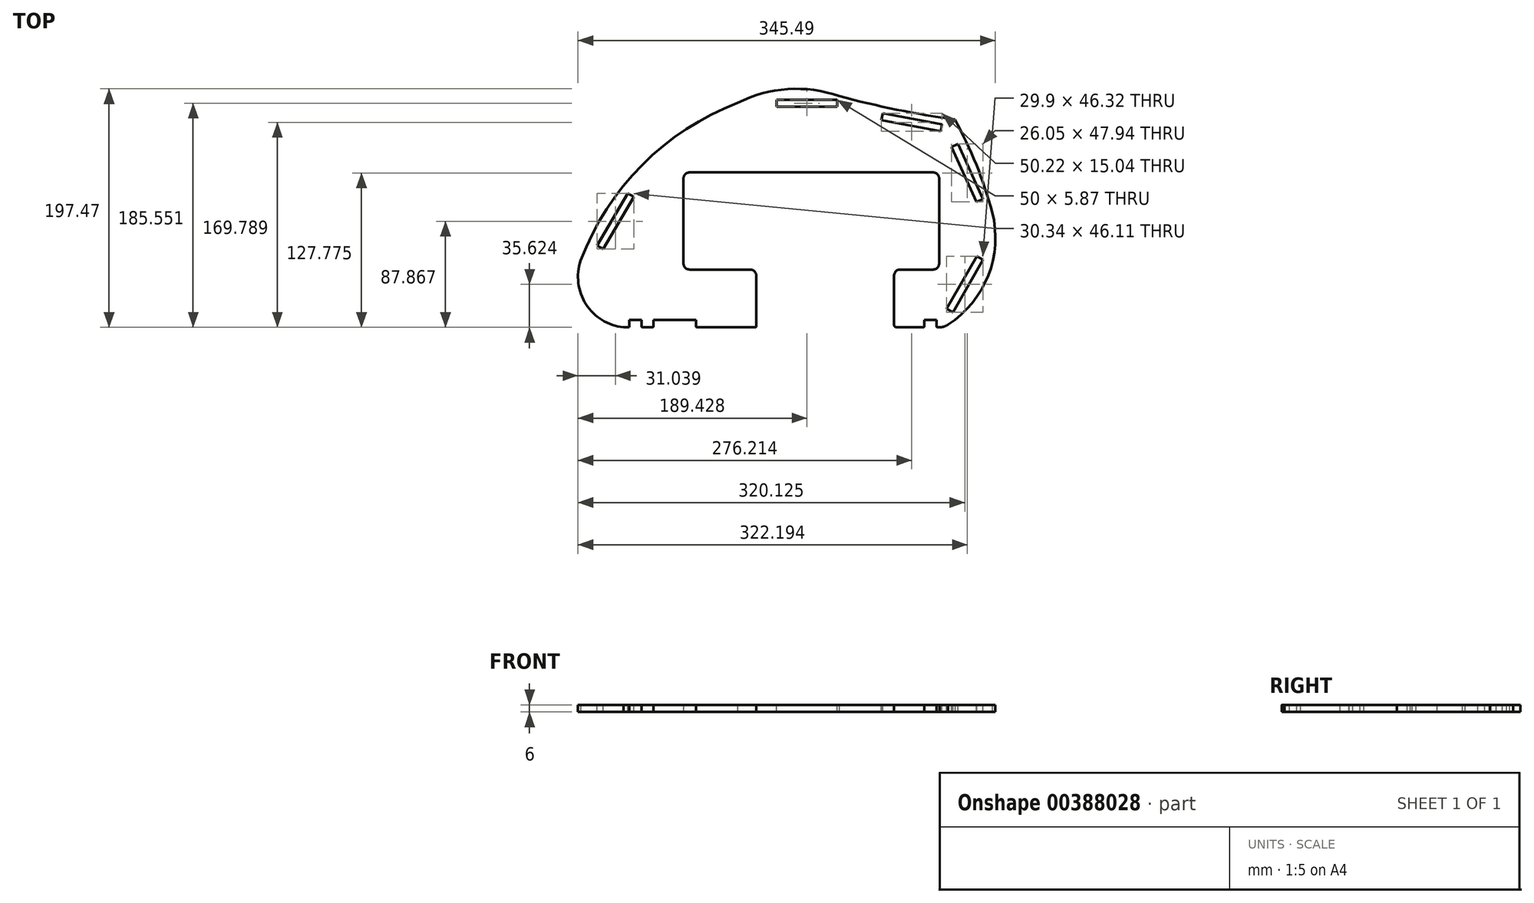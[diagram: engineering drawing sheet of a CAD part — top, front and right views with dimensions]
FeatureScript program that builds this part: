
annotation { "Feature Type Name" : "Feature", "Feature Type Description" : "" }
export const myFeature = defineFeature(function(context is Context, id is Id, definition is map)
    precondition{}
    {
        {
            var Q0;
            Q0=qCreatedBy(makeId("Top.planeOp"),FACE);
            var sketch = newSketch(context, id + "F0", { "sketchPlane" : qUnion([Q0])});
            skArc(sketch, "E0.0", {"start": v(177.07, -17.22) * mm, "mid": v(210.31, 23.38) * mm, "end": v(213.66, 75.75) * mm});
            skArc(sketch, "E1.0", {"start": v(170.2, -19.39) * mm, "mid": v(173.8, -18.84) * mm, "end": v(177.07, -17.22) * mm});
            skArc(sketch, "E2.0", {"start": v(-126.92, 35.78) * mm, "mid": v(-122.64, -0.38) * mm, "end": v(-91.61, -19.43) * mm});
            skArc(sketch, "E3.0", {"start": v(86.99, 172) * mm, "mid": v(44.36, 177.73) * mm, "end": v(2.91, 166.26) * mm});
            skArc(sketch, "E4", {"start": v(2.91, 166.26) * mm, "mid": v(-76.08, 115.03) * mm, "end": v(-126.92, 35.78) * mm});
            skArc(sketch, "E5", {"start": v(213.66, 75.75) * mm, "mid": v(200.48, 115.15) * mm, "end": v(182.68, 152.69) * mm});
            skLineSegment(sketch, "E6.0", {"start": v(157.44, -13.49) * mm, "end": v(157.44, -18.49) * mm});
            skLineSegment(sketch, "E7.0", {"start": v(132.44, -13.49) * mm, "end": v(132.44, -17.49) * mm});
            skLineSegment(sketch, "E8.0", {"start": v(-31.66, -13.49) * mm, "end": v(-31.66, -18.49) * mm});
            skLineSegment(sketch, "E8.1", {"start": v(-76.66, -13.49) * mm, "end": v(-76.66, -18.49) * mm});
            skLineSegment(sketch, "E9.0", {"start": v(-66.66, -13.49) * mm, "end": v(-66.66, -18.49) * mm});
            skLineSegment(sketch, "E9.1", {"start": v(18.34, -13.49) * mm, "end": v(18.34, -18.49) * mm});
            skLineSegment(sketch, "E10.0", {"start": v(167.44, -18.45) * mm, "end": v(167.44, -13.49) * mm});
            skLineSegment(sketch, "E11.0", {"start": v(-86.66, -13.49) * mm, "end": v(-86.66, -19.49) * mm});
            skLineSegment(sketch, "E12", {"start": v(167.44, -13.49) * mm, "end": v(157.44, -13.49) * mm});
            skLineSegment(sketch, "E13", {"start": v(-31.66, -13.49) * mm, "end": v(-66.66, -13.49) * mm});
            skLineSegment(sketch, "E14", {"start": v(-76.66, -13.49) * mm, "end": v(-86.66, -13.49) * mm});
            skLineSegment(sketch, "E15", {"start": v(170.2, -19.39) * mm, "end": v(168.47, -19.45) * mm});
            skLineSegment(sketch, "E16", {"start": v(156.44, -19.49) * mm, "end": v(134.44, -19.49) * mm});
            skLineSegment(sketch, "E17", {"start": v(-75.66, -19.49) * mm, "end": v(-67.66, -19.49) * mm});
            skLineSegment(sketch, "E18", {"start": v(-30.66, -19.49) * mm, "end": v(17.34, -19.49) * mm});
            skLineSegment(sketch, "E19", {"start": v(-91.61, -19.43) * mm, "end": v(-86.66, -19.49) * mm});
            skPoint(sketch, "E20.visualSharp", {"position": v(157.44, -19.49) * mm});
            skArc(sketch, "E20.filletArc", {"start": v(156.44, -19.49) * mm, "mid": v(157.15, -19.2) * mm, "end": v(157.44, -18.49) * mm});
            skPoint(sketch, "E21.visualSharp", {"position": v(132.44, -19.49) * mm});
            skArc(sketch, "E21.filletArc", {"start": v(132.44, -17.49) * mm, "mid": v(133.03, -18.9) * mm, "end": v(134.44, -19.49) * mm});
            skPoint(sketch, "E22.visualSharp", {"position": v(167.44, -19.49) * mm});
            skArc(sketch, "E22.filletArc", {"start": v(167.44, -18.45) * mm, "mid": v(167.75, -19.17) * mm, "end": v(168.47, -19.45) * mm});
            skPoint(sketch, "E23.visualSharp", {"position": v(-76.66, -19.49) * mm});
            skArc(sketch, "E23.filletArc", {"start": v(-76.66, -18.49) * mm, "mid": v(-76.37, -19.2) * mm, "end": v(-75.66, -19.49) * mm});
            skPoint(sketch, "E24.visualSharp", {"position": v(-66.66, -19.49) * mm});
            skArc(sketch, "E24.filletArc", {"start": v(-67.66, -19.49) * mm, "mid": v(-66.95, -19.2) * mm, "end": v(-66.66, -18.49) * mm});
            skPoint(sketch, "E25.visualSharp", {"position": v(-31.66, -19.49) * mm});
            skArc(sketch, "E25.filletArc", {"start": v(-31.66, -18.49) * mm, "mid": v(-31.37, -19.2) * mm, "end": v(-30.66, -19.49) * mm});
            skPoint(sketch, "E26.visualSharp", {"position": v(18.34, -19.49) * mm});
            skArc(sketch, "E26.filletArc", {"start": v(17.34, -19.49) * mm, "mid": v(18.05, -19.2) * mm, "end": v(18.34, -18.49) * mm});
            skLineSegment(sketch, "E27", {"start": v(132.44, -13.49) * mm, "end": v(132.44, 28.36) * mm});
            skLineSegment(sketch, "E28", {"start": v(132.44, 28.36) * mm, "end": v(169.69, 28.36) * mm});
            skLineSegment(sketch, "E29", {"start": v(169.69, 28.36) * mm, "end": v(169.69, 108.76) * mm});
            skLineSegment(sketch, "E30", {"start": v(-41.86, 28.36) * mm, "end": v(18.34, 28.36) * mm});
            skLineSegment(sketch, "E31", {"start": v(18.34, 28.36) * mm, "end": v(18.34, -13.49) * mm});
            skLineSegment(sketch, "E32", {"start": v(-41.86, 28.36) * mm, "end": v(-41.86, 108.76) * mm});
            skLineSegment(sketch, "E33", {"start": v(-41.86, 108.76) * mm, "end": v(169.69, 108.76) * mm});
            skArc(sketch, "E34", {"start": v(86.99, 172) * mm, "mid": v(134.51, 160.75) * mm, "end": v(182.68, 152.69) * mm});
            skSolve(sketch);
        }
        {
            var Q0;
            Q0 = qSketchRegion(id + "F0", true);
            extrude(context, id + "F1", {"entities" : qUnion([Q0]), "depth" : 6 * mm});
        }
        {
            var Q0;
            Q0=makeQuery(id+"F1.opExtrude","SWEPT_EDGE",EDGE,{"disambiguationData":[OSD([sQuery(id+"F0.wireOp",EDGE,"E32"),sQuery(id+"F0.wireOp",EDGE,"E33")])]});
            var Q1;
            Q1=makeQuery(id+"F1.opExtrude","SWEPT_EDGE",EDGE,{"disambiguationData":[OSD([sQuery(id+"F0.wireOp",EDGE,"E30"),sQuery(id+"F0.wireOp",EDGE,"E32")])]});
            var Q2;
            Q2=makeQuery(id+"F1.opExtrude","SWEPT_EDGE",EDGE,{"disambiguationData":[OSD([sQuery(id+"F0.wireOp",EDGE,"E30"),sQuery(id+"F0.wireOp",EDGE,"E31")])]});
            var Q3;
            Q3=makeQuery(id+"F1.opExtrude","SWEPT_EDGE",EDGE,{"disambiguationData":[OSD([sQuery(id+"F0.wireOp",EDGE,"E29"),sQuery(id+"F0.wireOp",EDGE,"E33")])]});
            var Q4;
            Q4=makeQuery(id+"F1.opExtrude","SWEPT_EDGE",EDGE,{"disambiguationData":[OSD([sQuery(id+"F0.wireOp",EDGE,"E28"),sQuery(id+"F0.wireOp",EDGE,"E29")])]});
            var Q5;
            Q5=makeQuery(id+"F1.opExtrude","SWEPT_EDGE",EDGE,{"disambiguationData":[OSD([sQuery(id+"F0.wireOp",EDGE,"E27"),sQuery(id+"F0.wireOp",EDGE,"E28")])]});
            fillet(context, id + "F2", {"entities" : qUnion([Q0, Q1, Q2, Q3, Q4, Q5]), "radius" : 5 * mm, "tangentPropagation" : true, "allowEdgeOverflow" : false});
        }
        {
            var Q0;
            Q0=makeQuery(id+"F1.opExtrude","CAP_FACE",FACE,{"disambiguationData":[OSD([sQuery(id+"F0.wireOp",EDGE,"E0.0"),sQuery(id+"F0.wireOp",EDGE,"E1.0"),sQuery(id+"F0.wireOp",EDGE,"E2.0"),sQuery(id+"F0.wireOp",EDGE,"E3.0"),sQuery(id+"F0.wireOp",EDGE,"623345de-7e64-4513-b3c6-34947c8a857b.0"),sQuery(id+"F0.wireOp",EDGE,"0303bcbb-beac-4a33-9d97-a44f9eb21fd0.0"),sQuery(id+"F0.wireOp",EDGE,"E4"),sQuery(id+"F0.wireOp",EDGE,"E5"),sQuery(id+"F0.wireOp",EDGE,"E6.0"),sQuery(id+"F0.wireOp",EDGE,"E7.0"),sQuery(id+"F0.wireOp",EDGE,"E8.0"),sQuery(id+"F0.wireOp",EDGE,"E8.1"),sQuery(id+"F0.wireOp",EDGE,"E9.0"),sQuery(id+"F0.wireOp",EDGE,"E9.1"),sQuery(id+"F0.wireOp",EDGE,"E10.0"),sQuery(id+"F0.wireOp",EDGE,"E11.0"),sQuery(id+"F0.wireOp",EDGE,"E12"),sQuery(id+"F0.wireOp",EDGE,"E13"),sQuery(id+"F0.wireOp",EDGE,"E14"),sQuery(id+"F0.wireOp",EDGE,"E15"),sQuery(id+"F0.wireOp",EDGE,"E16"),sQuery(id+"F0.wireOp",EDGE,"E17"),sQuery(id+"F0.wireOp",EDGE,"E18"),sQuery(id+"F0.wireOp",EDGE,"E19"),sQuery(id+"F0.wireOp",EDGE,"E20.filletArc"),sQuery(id+"F0.wireOp",EDGE,"E21.filletArc"),sQuery(id+"F0.wireOp",EDGE,"E22.filletArc"),sQuery(id+"F0.wireOp",EDGE,"E23.filletArc"),sQuery(id+"F0.wireOp",EDGE,"E24.filletArc"),sQuery(id+"F0.wireOp",EDGE,"E25.filletArc"),sQuery(id+"F0.wireOp",EDGE,"E26.filletArc"),sQuery(id+"F0.wireOp",EDGE,"E27"),sQuery(id+"F0.wireOp",EDGE,"E28"),sQuery(id+"F0.wireOp",EDGE,"E29"),sQuery(id+"F0.wireOp",EDGE,"E30"),sQuery(id+"F0.wireOp",EDGE,"E31"),sQuery(id+"F0.wireOp",EDGE,"E32"),sQuery(id+"F0.wireOp",EDGE,"E33")])],"isStart":false});
            var sketch = newSketch(context, id + "F3", { "sketchPlane" : qUnion([Q0])});
            skLineSegment(sketch, "E35", {"start": v(-113.35, 48.29) * mm, "end": v(-88.08, 91.43) * mm});
            skLineSegment(sketch, "E36", {"start": v(85.2, 169) * mm, "end": v(35.2, 169) * mm});
            skLineSegment(sketch, "E37", {"start": v(122.97, 157.82) * mm, "end": v(172.1, 148.55) * mm});
            skLineSegment(sketch, "E38", {"start": v(185.3, 132.26) * mm, "end": v(206, 86.74) * mm});
            skLineSegment(sketch, "E39", {"start": v(181.05, -7.03) * mm, "end": v(205.86, 36.38) * mm});
            skLineSegment(sketch, "E40.0", {"start": v(-108.28, 45.32) * mm, "end": v(-83.01, 88.47) * mm});
            skLineSegment(sketch, "E41.0", {"start": v(85.2, 163.13) * mm, "end": v(35.2, 163.13) * mm});
            skLineSegment(sketch, "E42.0", {"start": v(121.88, 152.05) * mm, "end": v(171.02, 142.78) * mm});
            skLineSegment(sketch, "E43.0", {"start": v(179.95, 129.83) * mm, "end": v(200.65, 84.31) * mm});
            skLineSegment(sketch, "E44.0", {"start": v(175.95, -4.12) * mm, "end": v(200.76, 39.3) * mm});
            skLineSegment(sketch, "E45", {"start": v(-108.28, 45.32) * mm, "end": v(-113.35, 48.29) * mm});
            skLineSegment(sketch, "E46", {"start": v(-83.01, 88.47) * mm, "end": v(-88.08, 91.43) * mm});
            skLineSegment(sketch, "E47", {"start": v(35.2, 163.13) * mm, "end": v(35.2, 169) * mm});
            skLineSegment(sketch, "E48", {"start": v(85.2, 163.13) * mm, "end": v(85.2, 169) * mm});
            skLineSegment(sketch, "E49", {"start": v(121.88, 152.05) * mm, "end": v(122.97, 157.82) * mm});
            skLineSegment(sketch, "E50", {"start": v(171.02, 142.78) * mm, "end": v(172.1, 148.55) * mm});
            skLineSegment(sketch, "E51", {"start": v(179.95, 129.83) * mm, "end": v(185.3, 132.26) * mm});
            skLineSegment(sketch, "E52", {"start": v(200.65, 84.31) * mm, "end": v(206, 86.74) * mm});
            skLineSegment(sketch, "E53", {"start": v(205.86, 36.38) * mm, "end": v(200.76, 39.3) * mm});
            skLineSegment(sketch, "E54", {"start": v(181.05, -7.03) * mm, "end": v(175.95, -4.12) * mm});
            skSolve(sketch);
        }
        {
            var Q0;
            Q0 = qSketchRegion(id + "F3", true);
            extrude(context, id + "F4", {"entities" : qUnion([Q0]), "operationType" : NewBodyOperationType.REMOVE, "oppositeDirection" : true, "depth" : 25 * mm});
        }
    });
